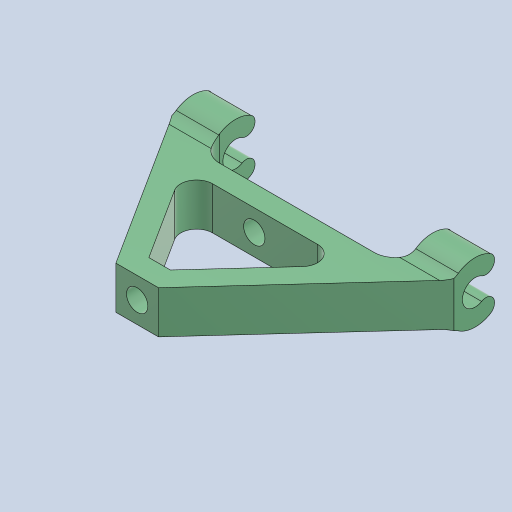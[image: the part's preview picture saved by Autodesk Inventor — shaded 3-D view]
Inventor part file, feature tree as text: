
AUTODESK INVENTOR PART (.ipt)
format: ipt  version: 2023 (Build 270158000, 158)  size: 227,328 bytes
history: native  units: mm
features: sketch x4, extrude x4, fillet x2, other x1, hole x1, mirror x1
ambient origin geometry x8: Origin, YZ Plane, XZ Plane, XY Plane, X Axis, Y Axis, Z Axis, Center Point
bodies: Body1 (feature_tree)
feature tree (13):
  other  "ソリッド1"
  sketch  "スケッチ1"
  extrude  "押し出し1"  Depth=4.0mm
  hole  "穴1"  [1 undecoded]
  sketch  "スケッチ4"
  extrude  "押し出し3"  Depth=16.5mm
  extrude  "押し出し4"  Depth=4.0mm TaperAngle=0.0deg
  mirror  "ミラー1"
  extrude  "押し出し5"  Depth=3.5mm
  fillet  "フィレット4"  Radius=2.4mm
  fillet  "フィレット5"  [1 undecoded]
  sketch  "スケッチ3"
  sketch  "スケッチ5"
note: 2 required parameter values undecoded (feature->parameter linkage not recoverable at this tier; creation-order binding heuristic only, values carry confidence <= 0.55)
